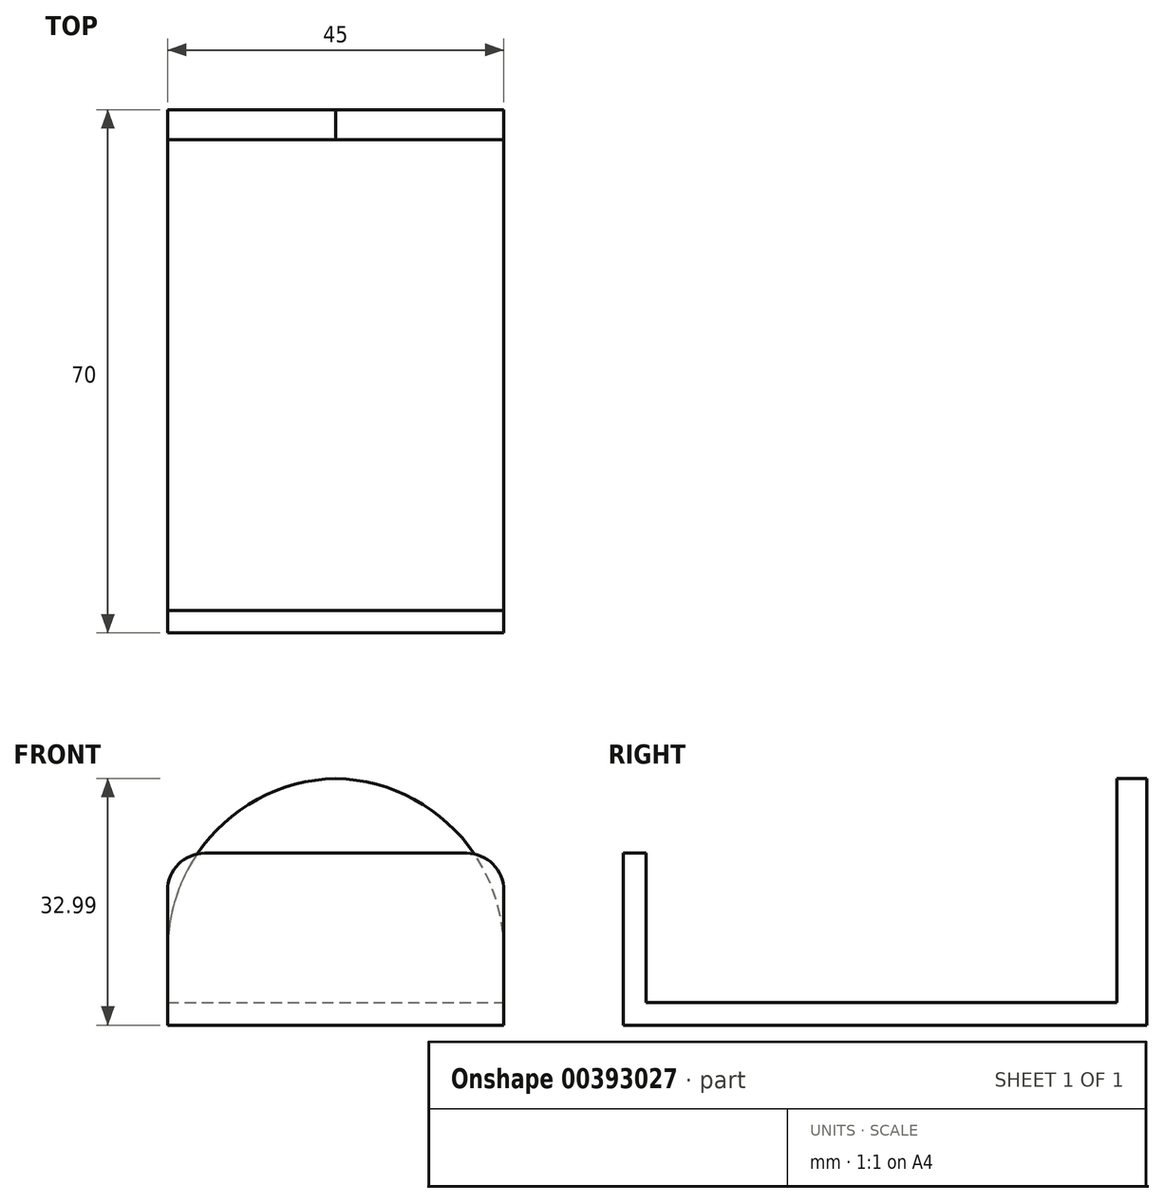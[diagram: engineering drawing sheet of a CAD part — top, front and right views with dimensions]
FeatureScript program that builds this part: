
annotation { "Feature Type Name" : "Feature", "Feature Type Description" : "" }
export const myFeature = defineFeature(function(context is Context, id is Id, definition is map)
    precondition{}
    {
        {
            var Q0;
            Q0=qCreatedBy(makeId("Top.planeOp"),FACE);
            var sketch = newSketch(context, id + "F0", { "sketchPlane" : qUnion([Q0])});
            skLineSegment(sketch, "E0.bottom", {"start": v(-22.5, 35) * mm, "end": v(22.5, 35) * mm});
            skLineSegment(sketch, "E0.top", {"start": v(-22.5, -35) * mm, "end": v(22.5, -35) * mm});
            skLineSegment(sketch, "E0.left", {"start": v(-22.5, 35) * mm, "end": v(-22.5, -35) * mm});
            skLineSegment(sketch, "E0.right", {"start": v(22.5, 35) * mm, "end": v(22.5, -35) * mm});
            skPoint(sketch, "E0.middle", {"position": v(0, 0) * mm});
            skSolve(sketch);
        }
        {
            var Q0;
            Q0=makeQuery(id+"F0.imprint","IMPRINT",FACE,{"disambiguationData":[TD([[makeQuery(id+"F0.imprint","IMPRINT",EDGE,{"derivedFrom":sQuery(id+"F0.wireOp",EDGE,"E0.bottom")}),-1.0]])]});
            extrude(context, id + "F1", {"entities" : qUnion([Q0]), "depth" : 3 * mm});
        }
        {
            var Q0;
            Q0=makeQuery(id+"F1.opExtrude","CAP_FACE",FACE,{"disambiguationData":[OSD([sQuery(id+"F0.wireOp",EDGE,"E0.bottom"),sQuery(id+"F0.wireOp",EDGE,"E0.top"),sQuery(id+"F0.wireOp",EDGE,"E0.left"),sQuery(id+"F0.wireOp",EDGE,"E0.right")])],"isStart":false});
            var sketch = newSketch(context, id + "F2", { "sketchPlane" : qUnion([Q0])});
            skLineSegment(sketch, "E1.bottom", {"start": v(-22.5, 35) * mm, "end": v(22.5, 35) * mm});
            skLineSegment(sketch, "E1.top", {"start": v(-22.5, 31) * mm, "end": v(22.5, 31) * mm});
            skLineSegment(sketch, "E1.left", {"start": v(-22.5, 35) * mm, "end": v(-22.5, 31) * mm});
            skLineSegment(sketch, "E1.right", {"start": v(22.5, 35) * mm, "end": v(22.5, 31) * mm});
            skSolve(sketch);
        }
        {
            var Q0;
            Q0=makeQuery(id+"F2.imprint","IMPRINT",FACE,{"disambiguationData":[TD([[makeQuery(id+"F2.imprint","IMPRINT",EDGE,{"derivedFrom":sQuery(id+"F2.wireOp",EDGE,"E1.bottom")}),-1.0]])]});
            extrude(context, id + "F3", {"entities" : qUnion([Q0]), "operationType" : NewBodyOperationType.ADD, "depth" : 30 * mm});
        }
        {
            var Q0;
            Q0=makeQuery(id+"F3.opExtrude","CAP_EDGE",EDGE,{"disambiguationData":[OSD([sQuery(id+"F2.wireOp",EDGE,"E1.left")])],"isStart":false});
            var Q1;
            Q1=makeQuery(id+"F3.opExtrude","CAP_EDGE",EDGE,{"disambiguationData":[OSD([sQuery(id+"F2.wireOp",EDGE,"E1.right")])],"isStart":false});
            fillet(context, id + "F4", {"entities" : qUnion([Q0, Q1]), "radius" : 23 * mm, "tangentPropagation" : true, "allowEdgeOverflow" : false});
        }
        {
            var Q0;
            Q0=makeQuery(id+"F1.opExtrude","CAP_FACE",FACE,{"disambiguationData":[OSD([sQuery(id+"F0.wireOp",EDGE,"E0.bottom"),sQuery(id+"F0.wireOp",EDGE,"E0.top"),sQuery(id+"F0.wireOp",EDGE,"E0.left"),sQuery(id+"F0.wireOp",EDGE,"E0.right")])],"isStart":false});
            var sketch = newSketch(context, id + "F5", { "sketchPlane" : qUnion([Q0])});
            skLineSegment(sketch, "E2.bottom", {"start": v(-22.5, -35) * mm, "end": v(22.5, -35) * mm});
            skLineSegment(sketch, "E2.top", {"start": v(-22.5, -32) * mm, "end": v(22.5, -32) * mm});
            skLineSegment(sketch, "E2.left", {"start": v(-22.5, -35) * mm, "end": v(-22.5, -32) * mm});
            skLineSegment(sketch, "E2.right", {"start": v(22.5, -35) * mm, "end": v(22.5, -32) * mm});
            skSolve(sketch);
        }
        {
            var Q0;
            Q0 = qSketchRegion(id + "F5", true);
            extrude(context, id + "F6", {"entities" : qUnion([Q0]), "operationType" : NewBodyOperationType.ADD, "depth" : 20 * mm});
        }
        {
            var Q0;
            Q0=makeQuery(id+"F6.opExtrude","CAP_EDGE",EDGE,{"disambiguationData":[OSD([sQuery(id+"F5.wireOp",EDGE,"E2.left")])],"isStart":false});
            var Q1;
            Q1=makeQuery(id+"F6.opExtrude","CAP_EDGE",EDGE,{"disambiguationData":[OSD([sQuery(id+"F5.wireOp",EDGE,"E2.right")])],"isStart":false});
            fillet(context, id + "F7", {"entities" : qUnion([Q0, Q1]), "radius" : 5 * mm, "tangentPropagation" : true, "allowEdgeOverflow" : false});
        }
    });
